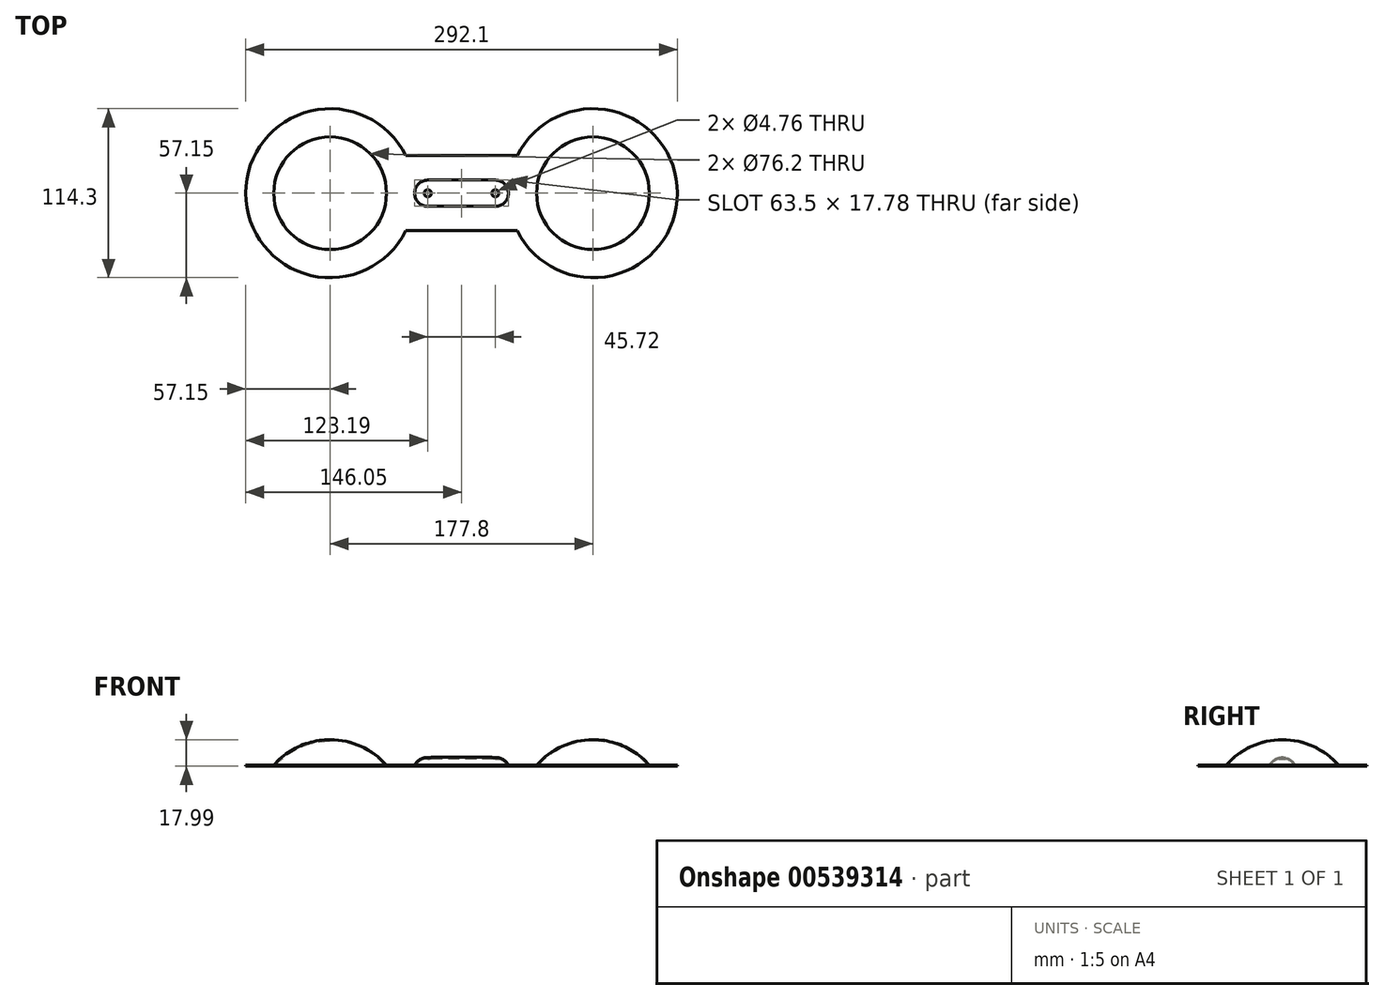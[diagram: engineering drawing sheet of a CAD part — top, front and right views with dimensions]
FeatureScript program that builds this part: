
annotation { "Feature Type Name" : "Feature", "Feature Type Description" : "" }
export const myFeature = defineFeature(function(context is Context, id is Id, definition is map)
    precondition{}
    {
        {
            var Q0;
            Q0=qCreatedBy(makeId("Top.planeOp"),FACE);
            var sketch = newSketch(context, id + "F0", { "sketchPlane" : qUnion([Q0])});
            skArc(sketch, "E0", {"start": v(-37.7, 25.4) * mm, "mid": v(-146.05, 0) * mm, "end": v(-37.7, -25.4) * mm});
            skLineSegment(sketch, "E1", {"start": v(-37.7, 25.4) * mm, "end": v(37.7, 25.4) * mm});
            skLineSegment(sketch, "E2", {"start": v(-37.7, -25.4) * mm, "end": v(37.7, -25.4) * mm});
            skArc(sketch, "E3", {"start": v(37.7, -25.4) * mm, "mid": v(146.05, 0) * mm, "end": v(37.7, 25.4) * mm});
            skPoint(sketch, "E4", {"position": v(-146.05, 0) * mm});
            skPoint(sketch, "E5", {"position": v(146.05, 0) * mm});
            skCircle(sketch, "E6", {"center": v(-88.9, 0) * mm, "radius": 38.1 * mm});
            skCircle(sketch, "E7", {"center": v(88.9, 0) * mm, "radius": 38.1 * mm});
            skLineSegment(sketch, "E8.bottom", {"start": v(22.86, 8.9) * mm, "end": v(-22.86, 8.89) * mm});
            skLineSegment(sketch, "E8.top", {"start": v(22.86, -8.89) * mm, "end": v(-22.86, -8.9) * mm});
            skLineSegment(sketch, "E8.left", {"start": v(31.75, 0) * mm, "end": v(31.75, 0) * mm});
            skLineSegment(sketch, "E8.right", {"start": v(-31.75, 0) * mm, "end": v(-31.75, 0) * mm});
            skPoint(sketch, "E8.middle", {"position": v(0, 0) * mm});
            skCircle(sketch, "E9", {"center": v(88.9, 0) * mm, "radius": 57.15 * mm, "construction": true});
            skPoint(sketch, "E10.visualSharp", {"position": v(-31.75, 8.89) * mm});
            skArc(sketch, "E10.filletArc", {"start": v(-22.86, 8.9) * mm, "mid": v(-29.15, 6.29) * mm, "end": v(-31.75, 0) * mm});
            skPoint(sketch, "E11.visualSharp", {"position": v(-31.75, -8.9) * mm});
            skArc(sketch, "E11.filletArc", {"start": v(-31.75, 0) * mm, "mid": v(-29.15, -6.29) * mm, "end": v(-22.86, -8.9) * mm});
            skPoint(sketch, "E12.visualSharp", {"position": v(31.75, -8.89) * mm});
            skArc(sketch, "E12.filletArc", {"start": v(22.86, -8.9) * mm, "mid": v(29.15, -6.29) * mm, "end": v(31.75, 0) * mm});
            skPoint(sketch, "E13.visualSharp", {"position": v(31.75, 8.9) * mm});
            skArc(sketch, "E13.filletArc", {"start": v(31.75, 0) * mm, "mid": v(29.15, 6.29) * mm, "end": v(22.86, 8.9) * mm});
            skSolve(sketch);
        }
        {
            var Q0;
            Q0=makeQuery(id+"F0.imprint","IMPRINT",FACE,{"disambiguationData":[TD([[makeQuery(id+"F0.imprint","IMPRINT",EDGE,{"derivedFrom":sQuery(id+"F0.wireOp",EDGE,"E0")}),1.0]])]});
            extrude(context, id + "F1", {"entities" : qUnion([Q0]), "oppositeDirection" : true, "depth" : 0.8 * mm, "offsetDistance" : 25.4 * mm});
        }
        {
            var Q0;
            Q0=qCreatedBy(makeId("Front.planeOp"),FACE);
            var sketch = newSketch(context, id + "F2", { "sketchPlane" : qUnion([Q0])});
            skLineSegment(sketch, "E14.0", {"start": v(-127, 0) * mm, "end": v(-50.8, 0) * mm, "construction": true});
            skLineSegment(sketch, "E15.0", {"start": v(50.8, 0) * mm, "end": v(127, 0) * mm, "construction": true});
            skArc(sketch, "E16", {"start": v(-88.9, 17.2) * mm, "mid": v(-109.8, 12.7) * mm, "end": v(-127, 0) * mm});
            skPoint(sketch, "E17", {"position": v(-88.9, 0) * mm});
            skArc(sketch, "E18.0", {"start": v(-88.9, 16.4) * mm, "mid": v(-109.47, 11.98) * mm, "end": v(-126.4, -0.53) * mm});
            skLineSegment(sketch, "E19", {"start": v(-88.9, 17.2) * mm, "end": v(-88.9, 16.4) * mm});
            skLineSegment(sketch, "E20", {"start": v(-127, 0) * mm, "end": v(-127, -0.8) * mm});
            skArc(sketch, "E21", {"start": v(-127, -0.8) * mm, "mid": v(-126.67, -0.72) * mm, "end": v(-126.4, -0.53) * mm});
            skLineSegment(sketch, "E22", {"start": v(-88.9, 17.2) * mm, "end": v(-88.9, 0) * mm, "construction": true});
            skSolve(sketch);
        }
        {
            var Q0;
            Q0 = qSketchRegion(id + "F2", true);
            var Q1;
            Q1=sQuery(id+"F2.wireOp",EDGE,"N75LoqFM-JiPO-zVKX-baJH-rTltWOZvRakT");
            var Q2;
            Q2=sQuery(id+"F2.wireOp",EDGE,"E22");
            revolve(context, id + "F3", {"surfaceOperationType" : NewSurfaceOperationType.NEW, "entities" : qUnion([Q0]), "surfaceEntities" : qUnion([Q1]), "axis" : qUnion([Q2]), "revolveType" : RevolveType.FULL});
        }
        {
            var Q0;
            Q0=makeQuery(id+"F3.opRevolve","SWEPT_BODY",BODY,{"disambiguationData":[OSD([sQuery(id+"F2.wireOp",EDGE,"E16"),sQuery(id+"F2.wireOp",EDGE,"E18.0"),sQuery(id+"F2.wireOp",EDGE,"E19"),sQuery(id+"F2.wireOp",EDGE,"E20"),sQuery(id+"F2.wireOp",EDGE,"E21")])]});
            var Q1;
            Q1=qCreatedBy(makeId("Right.planeOp"),FACE);
            mirror(context, id + "F4", {"entities" : qUnion([Q0]), "mirrorPlane" : qUnion([Q1])});
        }
        {
            var Q0;
            Q0=qCreatedBy(makeId("Right.planeOp"),FACE);
            var sketch = newSketch(context, id + "F5", { "sketchPlane" : qUnion([Q0])});
            skPoint(sketch, "E23.0", {"position": v(-8.9, 0) * mm});
            skArc(sketch, "E24", {"start": v(0, 5.24) * mm, "mid": v(-5.16, 3.83) * mm, "end": v(-8.9, 0) * mm});
            skArc(sketch, "E25.0", {"start": v(0, 4.45) * mm, "mid": v(-4.76, 3.15) * mm, "end": v(-8.2, -0.38) * mm});
            skLineSegment(sketch, "E26", {"start": v(0, 5.24) * mm, "end": v(0, 4.45) * mm});
            skLineSegment(sketch, "E27", {"start": v(-8.9, 0) * mm, "end": v(-8.9, -0.8) * mm});
            skArc(sketch, "E28", {"start": v(-8.9, -0.8) * mm, "mid": v(-8.49, -0.68) * mm, "end": v(-8.2, -0.38) * mm});
            skSolve(sketch);
        }
        {
            var Q0;
            Q0 = qSketchRegion(id + "F5", true);
            var Q1;
            Q1=sQuery(id+"F0.wireOp",EDGE,"E8.top");
            var Q2;
            Q2=sQuery(id+"F0.wireOp",EDGE,"E11.filletArc");
            var Q3;
            Q3=sQuery(id+"F0.wireOp",EDGE,"E10.filletArc");
            var Q4;
            Q4=sQuery(id+"F0.wireOp",EDGE,"E8.bottom");
            var Q5;
            Q5=sQuery(id+"F0.wireOp",EDGE,"E13.filletArc");
            var Q6;
            Q6=sQuery(id+"F0.wireOp",EDGE,"E12.filletArc");
            sweep(context, id + "F6", {"profiles" : qUnion([Q0]), "path" : qUnion([Q1, Q2, Q3, Q4, Q5, Q6])});
        }
        {
            var Q0;
            Q0=sQuery(id+"F0.wireOp",VERTEX,"E10.filletArc.center");
            var Q1;
            Q1=sQuery(id+"F0.wireOp",VERTEX,"E12.filletArc.center");
            var Q2;
            Q2=makeQuery(id+"F6.opSweep","SWEPT_BODY",BODY,{"disambiguationData":[OSD([sQuery(id+"F0.wireOp",EDGE,"E12.filletArc"),sQuery(id+"F5.wireOp",EDGE,"E24"),sQuery(id+"F5.wireOp",EDGE,"E25.0"),sQuery(id+"F5.wireOp",EDGE,"E26"),sQuery(id+"F5.wireOp",EDGE,"E27"),sQuery(id+"F5.wireOp",EDGE,"E28")])]});
            hole(context, id + "F7", {"style" : HoleStyle.SIMPLE, "endStyle" : HoleEndStyle.THROUGH, "oppositeDirection" : true, "holeDiameter" : 4.76 * mm, "majorDiameter" : 4.17 * mm, "isTappedThrough" : true, "tappedDepth" : 13.5 * mm, "tapClearance" : 3, "startFromSketch" : true, "locations" : qUnion([Q0, Q1]), "scope" : qUnion([Q2])});
        }
    });
